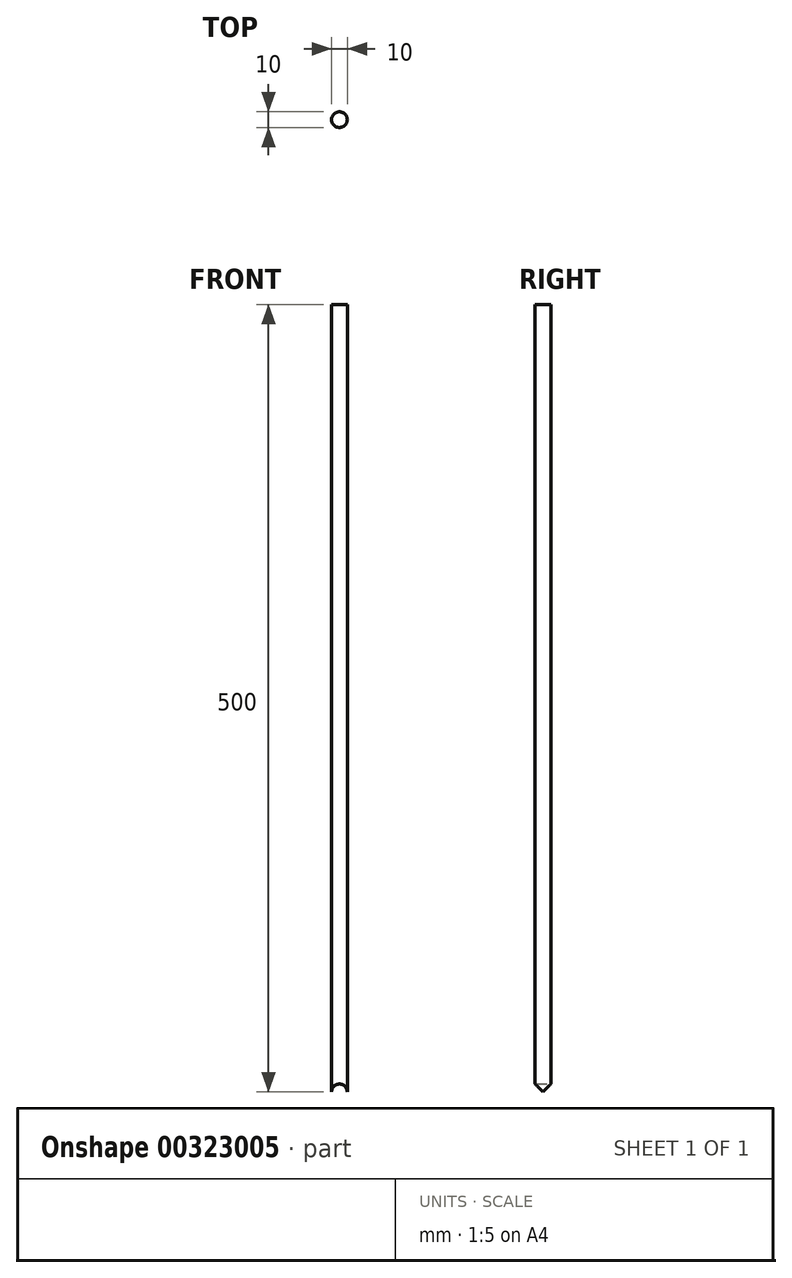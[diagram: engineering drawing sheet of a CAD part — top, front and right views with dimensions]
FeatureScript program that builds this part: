
annotation { "Feature Type Name" : "Feature", "Feature Type Description" : "" }
export const myFeature = defineFeature(function(context is Context, id is Id, definition is map)
    precondition{}
    {
        {
            var Q0;
            Q0=qCreatedBy(makeId("Top.planeOp"),FACE);
            var sketch = newSketch(context, id + "F0", { "sketchPlane" : qUnion([Q0])});
            skCircle(sketch, "E0", {"center": v(0, 0) * mm, "radius": 5 * mm});
            skSolve(sketch);
        }
        {
            var Q0;
            Q0 = qSketchRegion(id + "F0", true);
            extrude(context, id + "F1", {"entities" : qUnion([Q0]), "depth" : 500 * mm});
        }
        {
            var Q0;
            Q0=qCreatedBy(makeId("Top.planeOp"),FACE);
            var sketch = newSketch(context, id + "F2", { "sketchPlane" : qUnion([Q0])});
            skLineSegment(sketch, "E1.bottom", {"start": v(-5, -5) * mm, "end": v(0, -5) * mm});
            skLineSegment(sketch, "E1.top", {"start": v(-5, 5) * mm, "end": v(0, 5) * mm});
            skLineSegment(sketch, "E1.left", {"start": v(-5, -5) * mm, "end": v(-5, 5) * mm});
            skLineSegment(sketch, "E1.right", {"start": v(0, -5) * mm, "end": v(0, 5) * mm});
            skSolve(sketch);
        }
        {
            var Q0;
            Q0=makeQuery(id+"F2.imprint","IMPRINT",FACE,{"disambiguationData":[TD([[makeQuery(id+"F2.imprint","IMPRINT",EDGE,{"derivedFrom":sQuery(id+"F2.wireOp",EDGE,"E1.bottom")}),1.0]])]});
            var Q1;
            Q1=sQuery(id+"F2.wireOp",EDGE,"E1.right");
            revolve(context, id + "F3", {"operationType" : NewBodyOperationType.REMOVE, "entities" : qUnion([Q0]), "axis" : qUnion([Q1]), "revolveType" : RevolveType.FULL, "oppositeDirection" : true});
        }
    });
